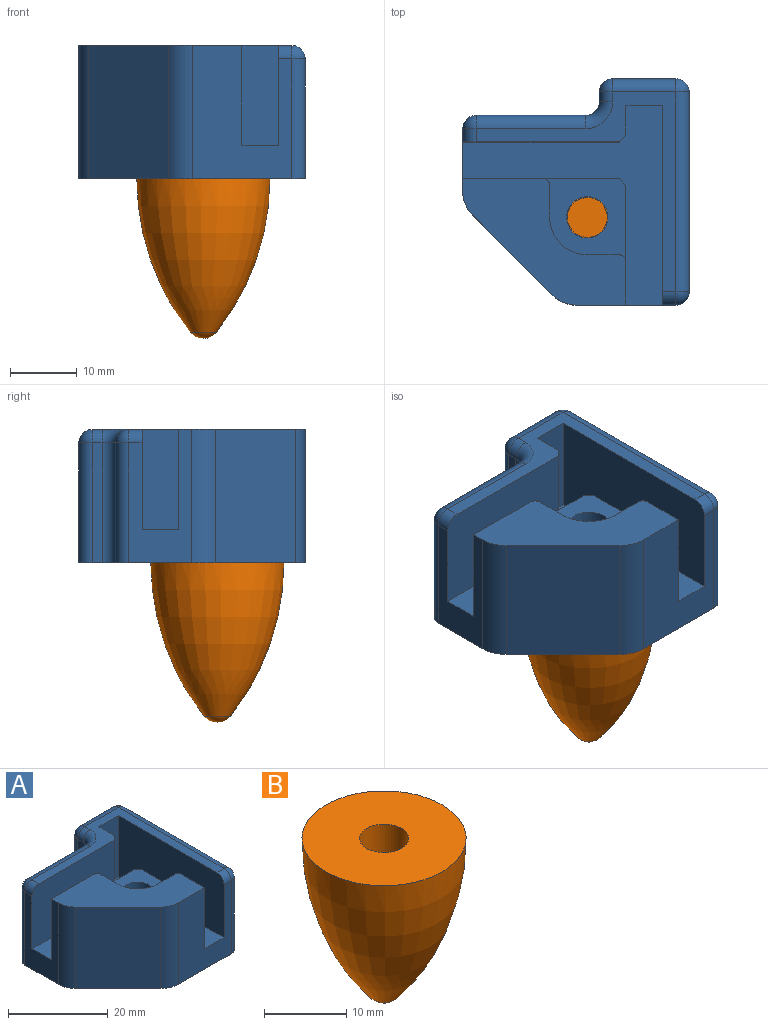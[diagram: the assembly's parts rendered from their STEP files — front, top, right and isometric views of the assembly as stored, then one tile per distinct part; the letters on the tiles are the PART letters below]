
ASSEMBLY  parts=2 mates=1
PART A: 44 faces, bbox 34x34x20 mm
  f0: plane 24.5x19mm, normal (0,0,1), area 227.2mm2, adj f1,f6,f7,f9,f34,f35,f36,f39
  f1: plane 23.5x15mm, normal (0,1,0), area 301mm2, adj f0,f2,f6,f14,f37,f39
  f2: plane 10.5x1mm, normal (0.71,0.71,0), area 14.8mm2, adj f1,f9,f14,f37
  f3: plane 18x9.5mm, normal (0,1,0), area 171mm2, adj f5,f18,f22,f27
  f4: plane 30x30mm, normal (0,0,1), area 129.9mm2, adj f10,f11,f12,f13,f15,f23,f25,f27
  f5: plane 34x34mm, normal (0,0,-1), area 896.9mm2, adj f3,f6,f7,f8,f16,f17,f18,f19
  f6: plane 20x9.43mm, normal (-1,0,0), area 102.1mm2, adj f0,f1,f5,f13,f14,f19,f33,f42
  f7: plane 20x14.93mm, normal (0,-1,0), area 212.1mm2, adj f0,f5,f9,f10,f14,f21,f23,f43
  f8: plane 30x18mm, normal (1,0,0), area 540mm2, adj f5,f21,f22,f25
  f9: plane 18x15mm, normal (1,0,0), area 218.5mm2, adj f0,f2,f7,f14,f37,f40
  f10: plane 30x15mm, normal (-1,0,0), area 449.1mm2, adj f4,f7,f11,f14,f23
  f11: plane 15x5.5mm, normal (0,-1,0), area 82.5mm2, adj f4,f10,f12,f14
  f12: plane 15x4.5mm, normal (1,0,0), area 67.5mm2, adj f4,f11,f14,f15
  f13: plane 23.5x15mm, normal (0,-1,0), area 351.6mm2, adj f4,f6,f14,f15,f33
  f14: plane 30x30mm, normal (0,0,1), area 300.7mm2, adj f1,f2,f6,f7,f9,f10,f11,f12
  f15: plane 15x1mm, normal (0.71,-0.71,0), area 21.2mm2, adj f4,f12,f13,f14
  f16: plane 18x1.5mm, normal (-1,0,0), area 27mm2, adj f5,f18,f20,f29
  f17: plane 18x16.5mm, normal (0,1,0), area 297mm2, adj f5,f19,f20,f31
  f18: cylinder r=2mm len=18mm, axis (0,0,1), area 56.5mm2, adj f3,f5,f16,f28
  f19: cylinder r=2mm len=18mm, axis (0,0,-1), area 56.5mm2, adj f5,f6,f17,f32
  f20: cylinder r=2mm len=18mm, axis (0,0,1), area 56.5mm2, adj f5,f16,f17,f30
  f21: cylinder r=2mm len=18mm, axis (0,0,-1), area 56.5mm2, adj f5,f7,f8,f24
  f22: cylinder r=2mm len=18mm, axis (0,0,1), area 56.5mm2, adj f3,f5,f8,f26
  f23: cylinder r=2mm len=2mm, axis (-1,0,0), area 6.3mm2, adj f4,f7,f10,f24
  f24: sphere r=2mm, area 6.3mm2, adj f21,f23,f25
  f25: cylinder r=2mm len=30mm, axis (0,-1,0), area 94.2mm2, adj f4,f8,f24,f26
  f26: sphere r=2mm, area 6.3mm2, adj f22,f25,f27
  f27: cylinder r=2mm len=9.5mm, axis (1,0,0), area 29.8mm2, adj f3,f4,f26,f28
  f28: sphere r=2mm, area 6.3mm2, adj f18,f27,f29
  f29: cylinder r=2mm len=2mm, axis (0,-1,0), area 4.7mm2, adj f4,f16,f28,f30
  f30: torus R=4mm, axis (0,0,1), area 13.5mm2, adj f4,f20,f29,f31
  f31: cylinder r=2mm len=16.5mm, axis (-1,0,0), area 51.8mm2, adj f4,f17,f30,f32
  f32: sphere r=2mm, area 6.3mm2, adj f19,f31,f33
  f33: cylinder r=2mm len=2mm, axis (0,1,0), area 6.3mm2, adj f4,f6,f13,f32
  f34: plane 4.8x4.5mm, normal (1,0,0), area 21.6mm2, adj f0,f35,f37,f39
  f35: cylinder r=5.65mm len=5.65mm, axis (0,0,1), area 39.9mm2, adj f0,f34,f36,f37
  f36: plane 4.8x4.5mm, normal (0,1,0), area 21.6mm2, adj f0,f35,f37,f40
  f37: plane 12.45x12.45mm, normal (0,0,1), area 94.1mm2, adj f1,f2,f9,f34,f35,f36,f38,f39
  f38: cylinder r=3.1mm len=15.5mm, axis (0,0,1), area 301.9mm2, adj f5,f37
  f39: cylinder r=1mm len=4.5mm, axis (0,0,-1), area 7.1mm2, adj f0,f1,f34,f37
  f40: cylinder r=1mm len=4.5mm, axis (0,0,1), area 7.1mm2, adj f0,f9,f36,f37
  f41: plane 20x12.07mm, normal (-0.71,-0.71,0), area 341.4mm2, adj f0,f5,f42,f43
  f42: cylinder r=5mm len=20mm, axis (0,0,1), area 78.5mm2, adj f0,f5,f6,f41
  f43: cylinder r=5mm len=20mm, axis (0,0,1), area 78.5mm2, adj f0,f5,f7,f41
PART B: 5 faces, bbox 20x20x24 mm
  f0: sphere r=2.5mm, area 14.8mm2, adj f1
  f1: revolved ~23.06x20mm, area 1137.9mm2, adj f0,f2
  f2: plane 20x20mm, normal (0,0,1), area 285.9mm2, adj f1,f3
  f3: cylinder r=3mm len=6mm, axis (0,0,1), area 113.1mm2, adj f2,f4
  f4: plane 6x6mm, normal (0,0,1), area 28.3mm2, adj f3
PLACE A at identity fixed
PLACE B t=(18.7,13.2,0)mm
MATE fastened B.f3 <-> A.f35  axis (0,0,1) through (18.7,13.2,0)mm
